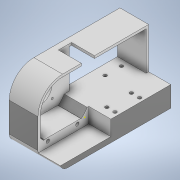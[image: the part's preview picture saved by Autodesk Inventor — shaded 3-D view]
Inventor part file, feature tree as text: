
AUTODESK INVENTOR PART (.ipt)
format: ipt  version: 2022 (Build 260153000, 153)  size: 1,397,248 bytes
history: mixed  units: mm
features: sketch x32, extrude x31, other x3, fillet x2, plane x1, imported_body x1
ambient origin geometry x8: Origin, YZ Plane, XZ Plane, XY Plane, X Axis, Y Axis, Z Axis, Center Point
bodies: Solid1 (imported_parasolid)
feature tree (70):
  other  "Assembly2.iam"
  other  "96Gears_Stage_1_modified.ipt:1"
  other  "96Gears_Stage_2_modified.ipt:1"
  extrude  "Extrusion3"  Depth=3.0mm
  extrude  "Extrusion5"  Depth=18.0mm TaperAngle=0.0deg
  extrude  "Extrusion6"  Depth=6.0mm TaperAngle=0.0deg
  extrude  "Extrusion7"  Depth=10.0mm TaperAngle=0.0deg
  extrude  "Extrusion8"  Depth=4.1mm
  extrude  "Extrusion9"  Depth=7.0mm
  extrude  "Extrusion10"  Depth=50.0mm TaperAngle=0.0deg
  extrude  "Extrusion11"  Depth=50.0mm TaperAngle=0.0deg
  extrude  "Extrusion12"  Depth=3.0mm TaperAngle=0.0deg
  extrude  "Extrusion13"  Depth=3.0mm TaperAngle=0.0deg
  extrude  "Extrusion14"  Depth=3.0mm TaperAngle=0.0deg
  extrude  "Extrusion15"  Depth=9.0mm TaperAngle=0.0deg
  extrude  "Extrusion16"  Depth=30.0mm
  fillet  "Fillet1"  Radius=5.0mm
  extrude  "Extrusion17"  Depth=10.0mm TaperAngle=0.0deg
  extrude  "Extrusion18"  Depth=10.0mm TaperAngle=0.0deg
  extrude  "Extrusion19"  Depth=1.25mm
  extrude  "Extrusion20"  Depth=10.0mm TaperAngle=0.0deg
  extrude  "Extrusion21"  Depth=10.0mm TaperAngle=0.0deg
  extrude  "Extrusion22"  Depth=10.0mm TaperAngle=0.0deg
  plane  "Work Plane1"
  extrude  "Extrusion26"  Depth=10.0mm TaperAngle=0.0deg
  extrude  "Extrusion27"  Depth=10.0mm
  extrude  "Extrusion28"  Depth=10.0mm TaperAngle=0.0deg
  extrude  "Extrusion29"  Depth=10.0mm TaperAngle=0.0deg
  extrude  "Extrusion30"  Depth=25.0mm TaperAngle=0.0deg
  extrude  "Extrusion31"  Depth=25.0mm
  extrude  "Extrusion32"  Depth=4.1mm
  extrude  "Extrusion33"  Depth=25.0mm
  extrude  "Extrusion34"  Depth=4.1mm
  extrude  "Extrusion35"  Depth=10.0mm
  extrude  "Extrusion36"  [1 undecoded]
  extrude  "Extrusion37"  [1 undecoded]
  fillet  "Fillet2"  [1 undecoded]
  sketch  "Sketch5"  dims[d7=6.0mm d8=18.0mm d9=0.0mm]
  sketch  "Sketch4"  dims[d0=10.0mm d6=3.0mm]
  sketch  "Sketch7"  dims[d17=32.25mm d18=6.0mm d19=0.0mm]
  sketch  "Sketch8"  dims[d20=10.0mm d21=10.0mm d22=0.0mm]
  sketch  "Sketch9"  dims[d24=4.1mm d25=4.1mm]
  sketch  "Sketch10"  dims[d26=10.0mm d27=0.0mm d28=7.0mm]
  sketch  "Sketch11"  dims[d29=0.0mm d30=0.0mm d31=50.0mm d32=0.0mm]
  sketch  "Sketch12"  dims[d33=3.0mm d34=50.0mm d35=0.0mm]
  sketch  "Sketch13"  dims[d38=3.0mm d39=3.0mm d40=0.0mm]
  sketch  "Sketch14"  dims[d41=23.0mm d42=3.0mm d43=0.0mm]
  sketch  "Sketch15"  dims[d44=3.0mm d45=0.0mm d46=9.0mm d47=0.0mm]
  sketch  "Sketch16"  dims[d49=33.25mm d50=9.0mm d51=0.0mm]
  sketch  "Sketch17"  dims[d52=2.0mm d53=0.0mm d54=30.0mm d55=5.0mm]
  sketch  "Sketch18"  dims[d57=5.0mm d58=10.0mm d59=0.0mm]
  sketch  "Sketch19"  dims[d60=3.0mm d61=10.0mm d62=0.0mm]
  sketch  "Sketch20"  dims[d63=2.0mm d64=0.0mm d65=1.25mm]
  sketch  "Sketch21"  dims[d66=2.0mm d67=0.0mm d68=10.0mm d69=0.0mm]
  sketch  "Sketch22"  dims[d74=2.5mm d75=10.0mm d76=0.0mm]
  sketch  "Sketch23"  dims[d98=10.0mm d99=0.0mm d100=10.0mm d101=0.0mm]
  sketch  "Sketch25"  dims[d102=10.0mm d103=0.0mm d104=10.0mm d105=0.0mm]
  sketch  "Sketch29"  dims[d106=10.0mm d107=0.0mm d108=8.0mm]
  sketch  "Sketch30"  dims[d109=16.0mm d110=10.0mm d111=0.0mm]
  sketch  "Sketch31"  dims[d112=2.5mm d114=10.0mm d115=0.0mm]
  sketch  "Sketch32"  dims[d116=10.0mm d117=0.0mm d118=25.0mm d119=0.0mm]
  sketch  "Sketch33"  dims[d120=25.0mm d121=0.0mm d122=12.5mm]
  sketch  "Sketch34"  dims[d123=1.5mm d124=4.1mm]
  sketch  "Sketch35"  dims[d125=0.0mm d126=0.0mm d128=25.0mm]
  sketch  "Sketch36"  dims[d129=12.865mm d133=4.1mm]
  sketch  "Sketch37"  dims[d134=10.0mm d135=0.0mm d136=4.1mm]
  sketch  "Sketch38"  dims[d137=9.25mm]
  sketch  "Sketch39"
  sketch  "Sketch40"
  imported_body  NMx_Import_Brep_tag  [imported B-rep: ~47 faces, bbox_mm=[62.0, 75.0, 135.0]]
note: 3 required parameter values undecoded (feature->parameter linkage not recoverable at this tier; creation-order binding heuristic only, values carry confidence <= 0.55)
